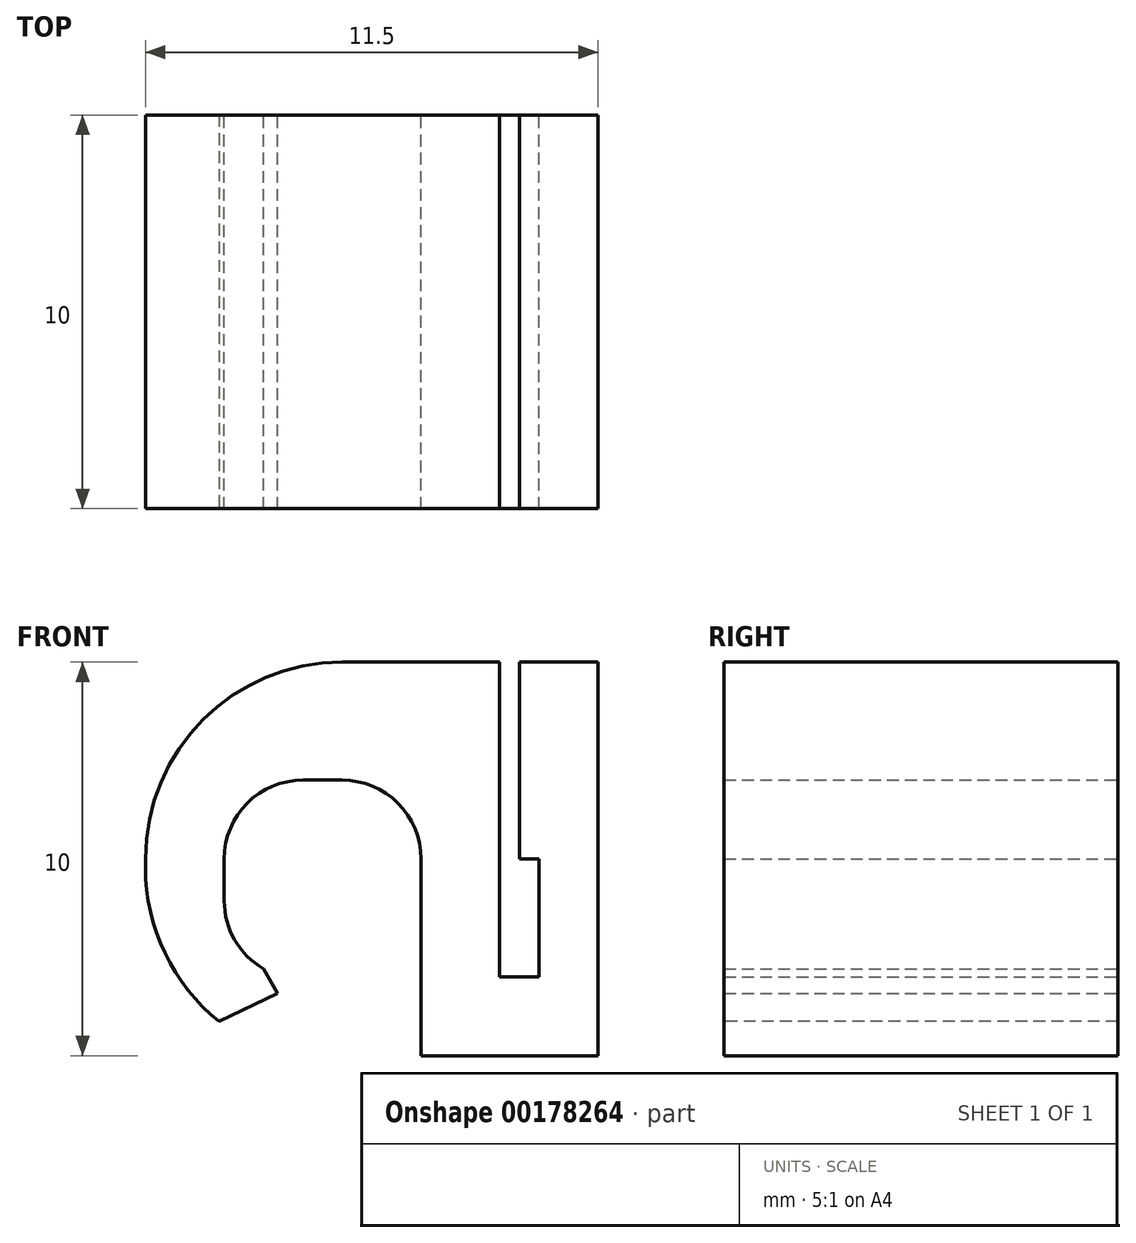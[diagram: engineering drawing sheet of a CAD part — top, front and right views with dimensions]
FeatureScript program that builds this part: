
annotation { "Feature Type Name" : "Feature", "Feature Type Description" : "" }
export const myFeature = defineFeature(function(context is Context, id is Id, definition is map)
    precondition{}
    {
        {
            var Q0;
            Q0=qCreatedBy(makeId("Front.planeOp"),FACE);
            var sketch = newSketch(context, id + "F0", { "sketchPlane" : qUnion([Q0])});
            skLineSegment(sketch, "E0", {"start": v(9, 10) * mm, "end": v(9, 2) * mm});
            skLineSegment(sketch, "E1", {"start": v(9, 2) * mm, "end": v(10, 2) * mm});
            skLineSegment(sketch, "E2", {"start": v(10, 2) * mm, "end": v(10, 5) * mm});
            skLineSegment(sketch, "E3", {"start": v(10, 5) * mm, "end": v(9.5, 5) * mm});
            skLineSegment(sketch, "E4", {"start": v(9.5, 5) * mm, "end": v(9.5, 10) * mm});
            skLineSegment(sketch, "E5", {"start": v(9.5, 10) * mm, "end": v(11.5, 10) * mm});
            skLineSegment(sketch, "E6", {"start": v(11.5, 10) * mm, "end": v(11.5, 0) * mm});
            skLineSegment(sketch, "E7", {"start": v(11.5, 0) * mm, "end": v(7, 0) * mm});
            skLineSegment(sketch, "E8", {"start": v(9, 10) * mm, "end": v(0, 10) * mm});
            skLineSegment(sketch, "E9", {"start": v(0, 10) * mm, "end": v(0, 0) * mm});
            skLineSegment(sketch, "E10", {"start": v(0, 0) * mm, "end": v(3.5, 0) * mm});
            skLineSegment(sketch, "E11", {"start": v(3.5, 0) * mm, "end": v(3.5, 2) * mm});
            skLineSegment(sketch, "E12", {"start": v(3.5, 2) * mm, "end": v(2, 2) * mm});
            skLineSegment(sketch, "E13", {"start": v(2, 2) * mm, "end": v(2, 7) * mm});
            skLineSegment(sketch, "E14", {"start": v(2, 7) * mm, "end": v(7, 7) * mm});
            skLineSegment(sketch, "E15", {"start": v(7, 7) * mm, "end": v(7, 0) * mm});
            skSolve(sketch);
        }
        {
            var Q0;
            Q0=makeQuery(id+"F0.imprint","IMPRINT",FACE,{"disambiguationData":[TD([[makeQuery(id+"F0.imprint","IMPRINT",EDGE,{"derivedFrom":sQuery(id+"F0.wireOp",EDGE,"E0")}),-1.0]])]});
            extrude(context, id + "F1", {"entities" : qUnion([Q0]), "depth" : 10 * mm});
        }
        {
            var Q0;
            Q0=makeQuery(id+"F1.opExtrude","SWEPT_EDGE",EDGE,{"disambiguationData":[OSD([sQuery(id+"F0.wireOp",EDGE,"E8"),sQuery(id+"F0.wireOp",EDGE,"E9")])]});
            var Q1;
            Q1=makeQuery(id+"F1.opExtrude","SWEPT_EDGE",EDGE,{"disambiguationData":[OSD([sQuery(id+"F0.wireOp",EDGE,"E9"),sQuery(id+"F0.wireOp",EDGE,"E10")])]});
            fillet(context, id + "F2", {"entities" : qUnion([Q0, Q1]), "radius" : 5 * mm, "tangentPropagation" : true, "allowEdgeOverflow" : false});
        }
        {
            var Q0;
            Q0=makeQuery(id+"F1.opExtrude","SWEPT_EDGE",EDGE,{"disambiguationData":[OSD([sQuery(id+"F0.wireOp",EDGE,"E12"),sQuery(id+"F0.wireOp",EDGE,"E13")])]});
            var Q1;
            Q1=makeQuery(id+"F1.opExtrude","SWEPT_EDGE",EDGE,{"disambiguationData":[OSD([sQuery(id+"F0.wireOp",EDGE,"E13"),sQuery(id+"F0.wireOp",EDGE,"E14")])]});
            var Q2;
            Q2=makeQuery(id+"F1.opExtrude","SWEPT_EDGE",EDGE,{"disambiguationData":[OSD([sQuery(id+"F0.wireOp",EDGE,"E14"),sQuery(id+"F0.wireOp",EDGE,"E15")])]});
            fillet(context, id + "F3", {"entities" : qUnion([Q0, Q1, Q2]), "radius" : 2 * mm, "tangentPropagation" : true, "allowEdgeOverflow" : false});
        }
        {
            var Q0;
            Q0=makeQuery(id+"F2.opFillet","BLEND_EDGE",EDGE,{"blendedFrom":[makeQuery(id+"F1.opExtrude","SWEPT_EDGE",EDGE,{"disambiguationData":[OSD([sQuery(id+"F0.wireOp",EDGE,"E9"),sQuery(id+"F0.wireOp",EDGE,"E10")])]}),makeQuery(id+"F1.opExtrude","SWEPT_FACE",FACE,{"disambiguationData":[OSD([sQuery(id+"F0.wireOp",EDGE,"E11")])]})],"blendedInto":[makeQuery(id+"F1.opExtrude","SWEPT_FACE",FACE,{"disambiguationData":[OSD([sQuery(id+"F0.wireOp",EDGE,"E11")])]})]});
            var Q1;
            Q1=makeQuery(id+"F1.opExtrude","SWEPT_EDGE",EDGE,{"disambiguationData":[OSD([sQuery(id+"F0.wireOp",EDGE,"E11"),sQuery(id+"F0.wireOp",EDGE,"E12")])]});
            var Q2;
            Q2=makeQuery(id+"F2.opFillet","BLEND_EDGE",EDGE,{"blendedFrom":[makeQuery(id+"F1.opExtrude","SWEPT_EDGE",EDGE,{"disambiguationData":[OSD([sQuery(id+"F0.wireOp",EDGE,"E6"),sQuery(id+"F0.wireOp",EDGE,"E7")])]}),makeQuery(id+"F1.opExtrude","SWEPT_FACE",FACE,{"disambiguationData":[OSD([sQuery(id+"F0.wireOp",EDGE,"E15")])]})],"blendedInto":[makeQuery(id+"F1.opExtrude","SWEPT_FACE",FACE,{"disambiguationData":[OSD([sQuery(id+"F0.wireOp",EDGE,"E15")])]})]});
            var Q3;
            Q3=makeQuery(id+"F3.opFillet","BLEND_EDGE",EDGE,{"blendedFrom":[makeQuery(id+"F1.opExtrude","SWEPT_EDGE",EDGE,{"disambiguationData":[OSD([sQuery(id+"F0.wireOp",EDGE,"E12"),sQuery(id+"F0.wireOp",EDGE,"E13")])]}),makeQuery(id+"F1.opExtrude","SWEPT_FACE",FACE,{"disambiguationData":[OSD([sQuery(id+"F0.wireOp",EDGE,"E11")])]})],"blendedInto":[makeQuery(id+"F1.opExtrude","SWEPT_FACE",FACE,{"disambiguationData":[OSD([sQuery(id+"F0.wireOp",EDGE,"E11")])]})]});
            chamfer(context, id + "F4", {"entities" : qUnion([Q0, Q1, Q2, Q3]), "width" : 1 * mm, "tangentPropagation" : true});
        }
    });
